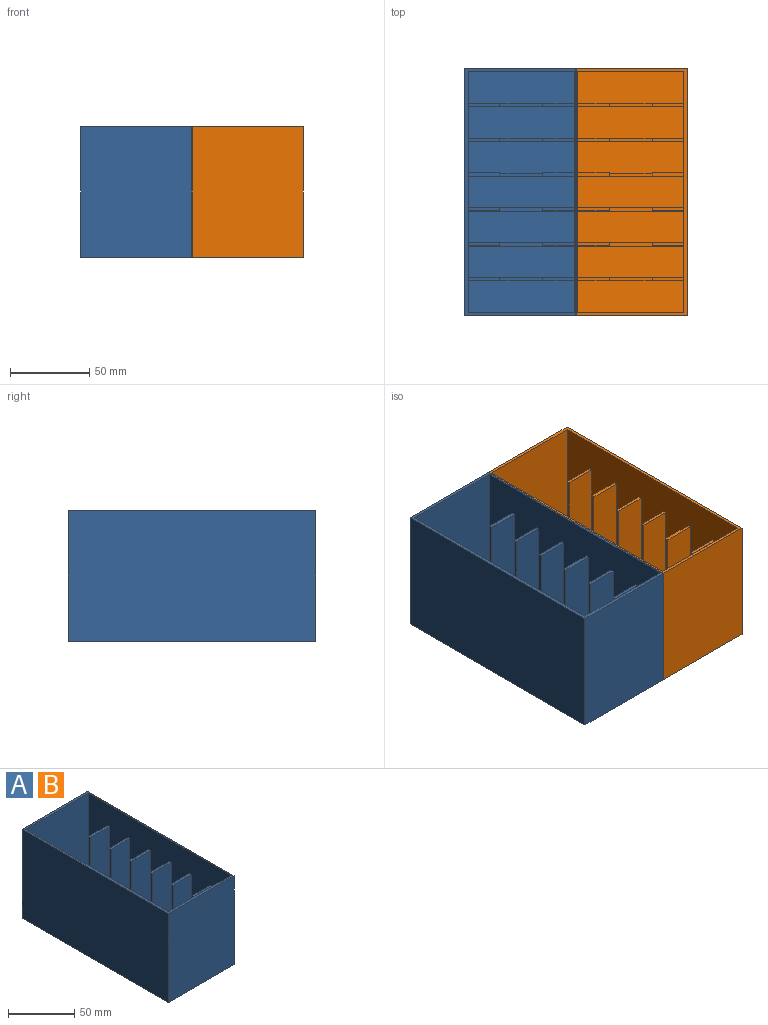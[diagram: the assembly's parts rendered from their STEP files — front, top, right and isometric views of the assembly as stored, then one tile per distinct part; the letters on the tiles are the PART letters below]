
ASSEMBLY  parts=2 mates=1
PART A: 59 faces, bbox 70x156x82 mm
  f0: plane 67x20mm, normal (0,0,1), area 1340mm2, adj f2,f6,f20,f33
  f1: plane 67x20mm, normal (0,0,1), area 1340mm2, adj f2,f6,f16,f21
  f2: plane 152x80mm, normal (1,0,0), area 11440mm2, adj f0,f1,f7,f8,f10,f12,f13,f16
  f3: plane 82x70mm, normal (0,1,0), area 5740mm2, adj f4,f9,f10,f56
  f4: plane 156x82mm, normal (-1,0,0), area 12792mm2, adj f3,f5,f10,f56
  f5: plane 82x70mm, normal (0,-1,0), area 5740mm2, adj f4,f9,f10,f56
  f6: plane 152x80mm, normal (-1,0,0), area 11440mm2, adj f0,f1,f7,f8,f10,f12,f13,f14
  f7: plane 80x67mm, normal (0,1,0), area 5360mm2, adj f2,f6,f10,f55
  f8: plane 80x67mm, normal (0,-1,0), area 5360mm2, adj f2,f6,f10,f49
  f9: plane 156x82mm, normal (1,0,0), area 12792mm2, adj f3,f5,f10,f56
  f10: plane 156x70mm, normal (0,0,1), area 736mm2, adj f2,f3,f4,f5,f6,f7,f8,f9
  f11: plane 50x2mm, normal (-1,0,0), area 100mm2, adj f12,f13,f14,f47
  f12: plane 67x60mm, normal (0,-1,0), area 2670mm2, adj f2,f6,f11,f14,f35,f36,f47,f52
  f13: plane 67x60mm, normal (0,1,0), area 2670mm2, adj f2,f6,f11,f14,f35,f36,f47,f50
  f14: plane 20x2mm, normal (0,0,1), area 40mm2, adj f6,f11,f12,f13
  f15: plane 50x2mm, normal (-1,0,0), area 100mm2, adj f16,f17,f18,f53
  f16: plane 67x60mm, normal (0,-1,0), area 2670mm2, adj f1,f2,f6,f15,f18,f41,f42,f53
  f17: plane 67x60mm, normal (0,1,0), area 2670mm2, adj f2,f6,f15,f18,f41,f42,f53,f54
  f18: plane 20x2mm, normal (0,0,1), area 40mm2, adj f6,f15,f16,f17
  f19: plane 50x2mm, normal (-1,0,0), area 100mm2, adj f20,f21,f22,f57
  f20: plane 67x60mm, normal (0,-1,0), area 2670mm2, adj f0,f2,f6,f19,f22,f45,f46,f57
  f21: plane 67x60mm, normal (0,1,0), area 2670mm2, adj f1,f2,f6,f19,f22,f45,f46,f57
  f22: plane 20x2mm, normal (0,0,1), area 40mm2, adj f6,f19,f20,f21
  f23: plane 50x2mm, normal (-1,0,0), area 100mm2, adj f24,f25,f26,f48
  f24: plane 67x60mm, normal (0,-1,0), area 2670mm2, adj f2,f6,f23,f26,f43,f44,f48,f50
  f25: plane 67x60mm, normal (0,1,0), area 2670mm2, adj f2,f6,f23,f26,f43,f44,f48,f49
  f26: plane 20x2mm, normal (0,0,1), area 40mm2, adj f6,f23,f24,f25
  f27: plane 50x2mm, normal (-1,0,0), area 100mm2, adj f28,f29,f30,f51
  f28: plane 67x60mm, normal (0,-1,0), area 2670mm2, adj f2,f6,f27,f30,f39,f40,f51,f54
  f29: plane 67x60mm, normal (0,1,0), area 2670mm2, adj f2,f6,f27,f30,f39,f40,f51,f52
  f30: plane 20x2mm, normal (0,0,1), area 40mm2, adj f6,f27,f28,f29
  f31: plane 50x2mm, normal (-1,0,0), area 100mm2, adj f32,f33,f34,f58
  f32: plane 67x60mm, normal (0,-1,0), area 2670mm2, adj f2,f6,f31,f34,f37,f38,f55,f58
  f33: plane 67x60mm, normal (0,1,0), area 2670mm2, adj f0,f2,f6,f31,f34,f37,f38,f58
  f34: plane 20x2mm, normal (0,0,1), area 40mm2, adj f6,f31,f32,f33
  f35: plane 50x2mm, normal (1,0,0), area 100mm2, adj f12,f13,f36,f47
  f36: plane 20x2mm, normal (0,0,1), area 40mm2, adj f2,f12,f13,f35
  f37: plane 50x2mm, normal (1,0,0), area 100mm2, adj f32,f33,f38,f58
  f38: plane 20x2mm, normal (0,0,1), area 40mm2, adj f2,f32,f33,f37
  f39: plane 50x2mm, normal (1,0,0), area 100mm2, adj f28,f29,f40,f51
  f40: plane 20x2mm, normal (0,0,1), area 40mm2, adj f2,f28,f29,f39
  f41: plane 50x2mm, normal (1,0,0), area 100mm2, adj f16,f17,f42,f53
  f42: plane 20x2mm, normal (0,0,1), area 40mm2, adj f2,f16,f17,f41
  f43: plane 50x2mm, normal (1,0,0), area 100mm2, adj f24,f25,f44,f48
  f44: plane 20x2mm, normal (0,0,1), area 40mm2, adj f2,f24,f25,f43
  f45: plane 50x2mm, normal (1,0,0), area 100mm2, adj f20,f21,f46,f57
  f46: plane 20x2mm, normal (0,0,1), area 40mm2, adj f2,f20,f21,f45
  f47: plane 27x2mm, normal (0,0,1), area 54mm2, adj f11,f12,f13,f35
  f48: plane 27x2mm, normal (0,0,1), area 54mm2, adj f23,f24,f25,f43
  f49: plane 67x20mm, normal (0,0,1), area 1340mm2, adj f2,f6,f8,f25
  f50: plane 67x20mm, normal (0,0,1), area 1340mm2, adj f2,f6,f13,f24
  f51: plane 27x2mm, normal (0,0,1), area 54mm2, adj f27,f28,f29,f39
  f52: plane 67x20mm, normal (0,0,1), area 1340mm2, adj f2,f6,f12,f29
  f53: plane 27x2mm, normal (0,0,1), area 54mm2, adj f15,f16,f17,f41
  f54: plane 67x20mm, normal (0,0,1), area 1340mm2, adj f2,f6,f17,f28
  f55: plane 67x20mm, normal (0,0,1), area 1340mm2, adj f2,f6,f7,f32
  f56: plane 156x70mm, normal (0,0,-1), area 10920mm2, adj f3,f4,f5,f9
  f57: plane 27x2mm, normal (0,0,1), area 54mm2, adj f19,f20,f21,f45
  f58: plane 27x2mm, normal (0,0,1), area 54mm2, adj f31,f32,f33,f37
PART B: same geometry as A
PLACE A t=(-54.93,-11.71,18.99)mm
PLACE B rot(axis=(0,0,1),180deg) t=(-5.64,13.64,18.99)mm
MATE fastened B.f3 <-> A.f5  axis (0,-1,0) through (-30.29,-77.03,16.99)mm
